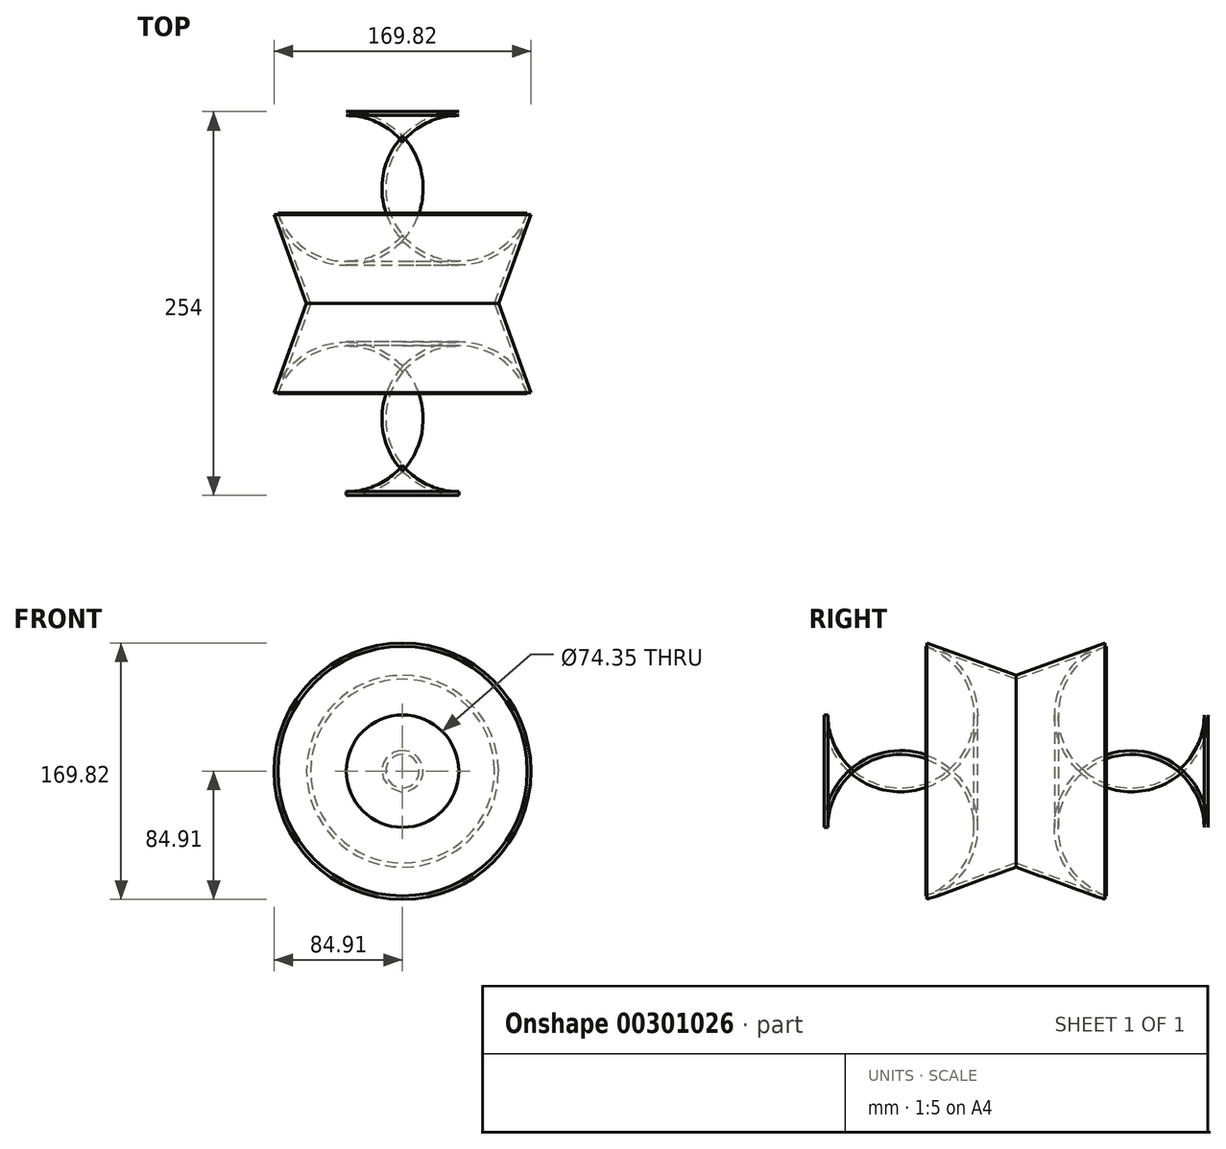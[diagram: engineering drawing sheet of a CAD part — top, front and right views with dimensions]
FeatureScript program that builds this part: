
annotation { "Feature Type Name" : "Feature", "Feature Type Description" : "" }
export const myFeature = defineFeature(function(context is Context, id is Id, definition is map)
    precondition{}
    {
        {
            var Q0;
            Q0=qCreatedBy(makeId("Front.planeOp"),FACE);
            var sketch = newSketch(context, id + "F0", { "sketchPlane" : qUnion([Q0])});
            skCircle(sketch, "E0", {"center": v(0, 0) * mm, "radius": 63.5 * mm});
            skSolve(sketch);
        }
        {
            var Q0;
            Q0=makeQuery(id+"F0.imprint","IMPRINT",FACE,{"disambiguationData":[TD([[makeQuery(id+"F0.imprint","IMPRINT",EDGE,{"derivedFrom":sQuery(id+"F0.wireOp",EDGE,"E0")}),1.0]])]});
            extrude(context, id + "F1", {"entities" : qUnion([Q0]), "endBound" : BoundingType.SYMMETRIC, "depth" : 254 * mm, "hasDraft" : true, "draftAngle" : 20 * degree});
        }
        {
            var Q0;
            Q0=makeQuery(id+"F1.opExtrude","CAP_FACE",FACE,{"disambiguationData":[OSD([sQuery(id+"F0.wireOp",EDGE,"E0")])],"isStart":false});
            var Q1;
            Q1=makeQuery(id+"F1.opExtrude","CAP_FACE",FACE,{"disambiguationData":[OSD([sQuery(id+"F0.wireOp",EDGE,"E0")])],"isStart":true});
            fillet(context, id + "F2", {"entities" : qUnion([Q0, Q1]), "radius" : 50.8 * mm, "tangentPropagation" : true, "allowEdgeOverflow" : false});
        }
        {
            var Q0;
            Q0=makeQuery(id+"F1.opExtrude","CAP_FACE",FACE,{"disambiguationData":[OSD([sQuery(id+"F0.wireOp",EDGE,"E0")])],"isStart":false});
            shell(context, id + "F3", {"entities" : qUnion([Q0]), "thickness" : 2.54 * mm});
        }
    });
